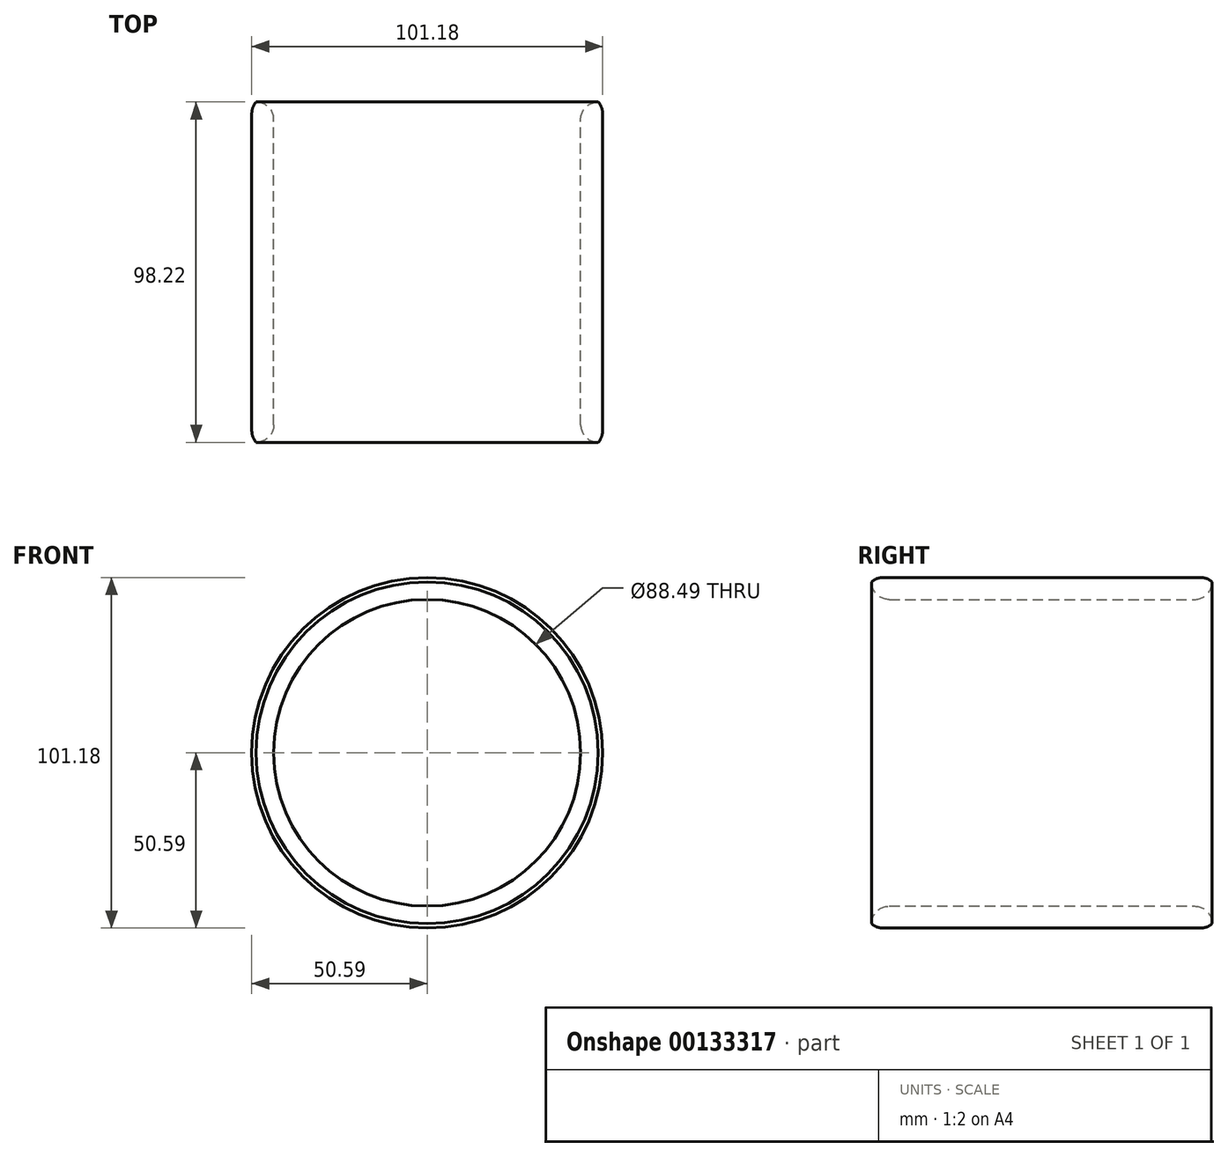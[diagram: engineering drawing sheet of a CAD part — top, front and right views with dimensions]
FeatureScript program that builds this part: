
annotation { "Feature Type Name" : "Feature", "Feature Type Description" : "" }
export const myFeature = defineFeature(function(context is Context, id is Id, definition is map)
    precondition{}
    {
        {
            var Q0;
            Q0=qCreatedBy(makeId("Front.planeOp"),FACE);
            var sketch = newSketch(context, id + "F0", { "sketchPlane" : qUnion([Q0])});
            skCircle(sketch, "E0", {"center": v(0, 0) * mm, "radius": 50.6 * mm});
            skCircle(sketch, "E1.0", {"center": v(0, 0) * mm, "radius": 44.24 * mm});
            skLineSegment(sketch, "E2", {"start": v(11.73, 49.22) * mm, "end": v(0, 0) * mm});
            skSolve(sketch);
        }
        {
            var Q0;
            Q0 = qSketchRegion(id + "F0", true);
            extrude(context, id + "F1", {"entities" : qUnion([Q0]), "depth" : 98.22 * mm});
        }
        {
            var Q0;
            Q0=makeQuery(id+"F1.opExtrude","CAP_EDGE",EDGE,{"disambiguationData":[OSD([sQuery(id+"F0.wireOp",EDGE,"E1.0")])],"isStart":false});
            fillet(context, id + "F2", {"entities" : qUnion([Q0]), "radius" : 5.08 * mm, "tangentPropagation" : true, "allowEdgeOverflow" : false});
        }
        {
            var Q0;
            Q0=makeQuery(id+"F1.opExtrude","CAP_EDGE",EDGE,{"disambiguationData":[OSD([sQuery(id+"F0.wireOp",EDGE,"E0")])],"isStart":false});
            fillet(context, id + "F3", {"entities" : qUnion([Q0]), "radius" : 5.08 * mm, "tangentPropagation" : true, "allowEdgeOverflow" : false});
        }
        {
            var Q0;
            Q0=makeQuery(id+"F1.opExtrude","CAP_EDGE",EDGE,{"disambiguationData":[OSD([sQuery(id+"F0.wireOp",EDGE,"E1.0")])],"isStart":true});
            fillet(context, id + "F4", {"entities" : qUnion([Q0]), "radius" : 5.08 * mm, "tangentPropagation" : true, "allowEdgeOverflow" : false});
        }
        {
            var Q0;
            Q0=makeQuery(id+"F1.opExtrude","CAP_EDGE",EDGE,{"disambiguationData":[OSD([sQuery(id+"F0.wireOp",EDGE,"E0")])],"isStart":true});
            fillet(context, id + "F5", {"entities" : qUnion([Q0]), "radius" : 5.08 * mm, "tangentPropagation" : true, "allowEdgeOverflow" : false});
        }
    });
